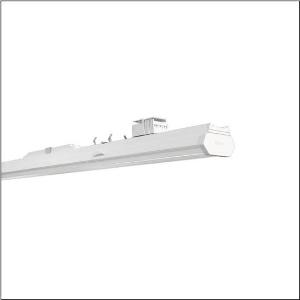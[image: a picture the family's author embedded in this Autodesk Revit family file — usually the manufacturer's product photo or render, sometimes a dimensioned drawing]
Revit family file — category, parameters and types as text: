
# Revit family: licross_11_protected_ho_51tp12cn3d5m
name_source: partatom
category: Lighting Fixtures
units: mm (PartAtom-declared; Revit-internal decimal feet)

## family parameters
Cut with Voids When Loaded = No
Host = Face
Light Source = No
Part Type = Normal
Room Calculation Point = No
Round Connector Dimension = Use Diameter
Shared = No

## types (1)
- --- (1 x LED, 13690 lm, 77.6 W, 3000K)
    Apparent Load = 78 VA
    CIE Flux Codes = 70 91 97 98 100
    Color Rendering = 80
    Color Temperature = 3000K
    Default Elevation = 1800 mm
    Description = Licross 11 Protected HO, luminaire insert, of sheet steel, galvanised, coil coated, white, length: 1.500mm, width: 90mm, height: 101mm, LED rated luminous flux: 13.690lm, light colour: 830, SDCM (Standard Deviation of Colour Matching)MacAdam ≤ 2 SDCM (initial), control gear: ON/OFF Multilumen, CLOi, with plug, 3-pole, with phase selection, mains connection: 220..240V, AC, 50/60Hz, start of lifetime: 78W, end of service life: 87W, internal wiring halogen-free, primary light control with lens, of plastic, primary optical cover: cover, of PMMA, light emission: direct distribution, primary light characteristic: symmetric, protection rating (complete): IP64, insulation class (complete): insulation class I (protective earthing), certification: CE, ENEC, VDE, UKCA, protection symbol: D if used in an environment with conductive dust loads with corresponding accessories, impact resistance: IK06, permissible ambient temperature for indoor applications: -35..+35°C, corresponds to IFS (International Featured Standards) requirements for safety and quality in the food industry, reducing of maximum allowable ambient temperature of 5°C with ceiling mounting, LABS conformity tested according to VDMA 24364:2018-05, The light source and the operating device comply with the requirements of the Ecodesign Regulation (EU) 2019/2020 and are replaceable in accordance with this regulation, packaging unit: 1 piece
    Height = 92 mm
    Lamp = 1 x LED
    Lamp Light Flux = 13690 lm
    Lamp Power = 77.6 W
    Lamp count = 1
    Length = 1500 mm
    Luminous efficacy = 176 lm/W
    Manufacturer = Siteco
    ModVariant = No
    Model = 51TP12CN3D5M
    Mounting Place = Ceiling
    Mounting Type = Pendant
    Number of Poles = 1
    OnlyDefault = Yes
    Power Factor = 1
    Product Name = Licross 11 Protected HO
    Product group = luminaire insert | ceiling pendant
    ProductGroupID = 901
    Protection Class = Protection class I
    Protection Degree = IP 64
    RLX_Detail_Level = 1
    RLX_Emergency_Light_Flux = 0 lm
    RLX_Emergency_Type = 0
    RLX_Emergency_Type_DB = No
    RlxData = <blob elided: 22501 chars, md5=89cc7004>
    Socket = socket
    Standby Power = 0 W
    System Light Flux = 13690 lm
    System Power = 78 W
    Type Comments = factory setting: luminous flux: 100 % | (A | C | E) | 181 mA
    Type Image = l_1256148.jpg
    URL = http://relux.com
    VarID = @adj_000919
    Voltage = 0 V
    Weight = 0.00 kg
    Width = 88 mm

## geometry (parser evidence)
native form markers: Blend x4, Sweep x12
no freeform markers — native parametric forms only
